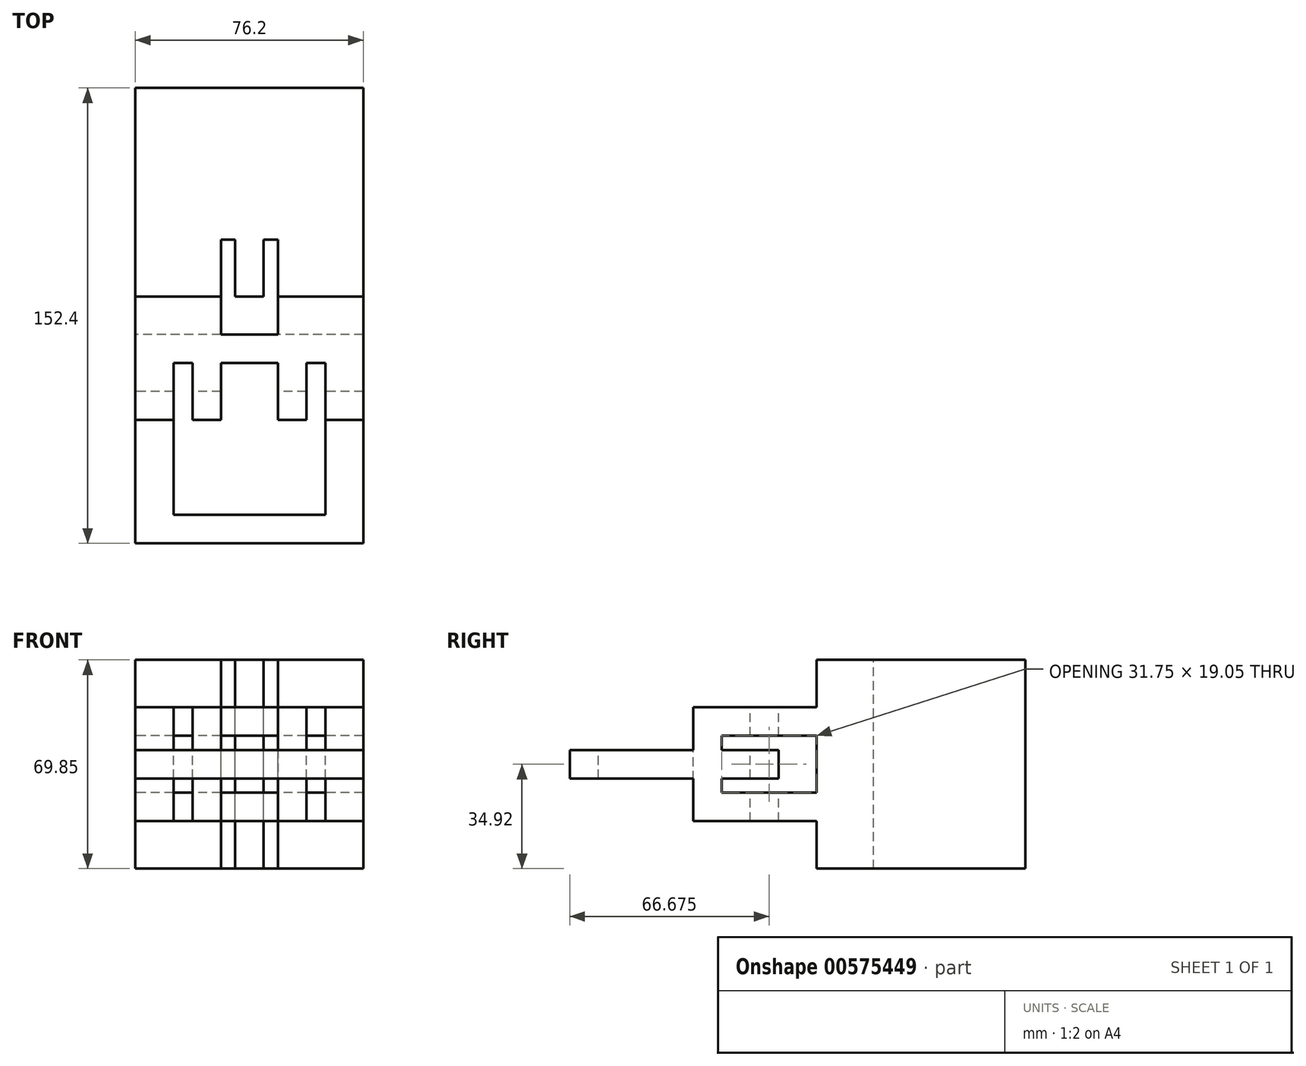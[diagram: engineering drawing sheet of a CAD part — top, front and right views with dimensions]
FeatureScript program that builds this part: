
annotation { "Feature Type Name" : "Feature", "Feature Type Description" : "" }
export const myFeature = defineFeature(function(context is Context, id is Id, definition is map)
    precondition{}
    {
        {
            var Q0;
            Q0=qCreatedBy(makeId("Top.planeOp"),FACE);
            var sketch = newSketch(context, id + "F0", { "sketchPlane" : qUnion([Q0])});
            skLineSegment(sketch, "E0.bottom", {"start": v(-38.1, 76.2) * mm, "end": v(38.1, 76.2) * mm});
            skLineSegment(sketch, "E0.top", {"start": v(-38.1, -76.2) * mm, "end": v(38.1, -76.2) * mm});
            skLineSegment(sketch, "E0.left", {"start": v(-38.1, 76.2) * mm, "end": v(-38.1, -76.2) * mm});
            skLineSegment(sketch, "E0.right", {"start": v(38.1, 76.2) * mm, "end": v(38.1, -76.2) * mm});
            skLineSegment(sketch, "E1", {"start": v(-38.1, 76.2) * mm, "end": v(38.1, -76.2) * mm, "construction": true});
            skSolve(sketch);
        }
        {
            var Q0;
            Q0=makeQuery(id+"F0.imprint","IMPRINT",FACE,{"disambiguationData":[TD([[makeQuery(id+"F0.imprint","IMPRINT",EDGE,{"derivedFrom":sQuery(id+"F0.wireOp",EDGE,"E0.bottom")}),-1.0]])]});
            extrude(context, id + "F1", {"entities" : qUnion([Q0]), "endBound" : BoundingType.SYMMETRIC, "oppositeDirection" : true, "depth" : 76.2 * mm, "offsetDistance" : 25.4 * mm});
        }
        {
            var Q0;
            Q0=makeQuery(id+"F1.opExtrude","CAP_FACE",FACE,{"disambiguationData":[OSD([sQuery(id+"F0.wireOp",EDGE,"E0.bottom"),sQuery(id+"F0.wireOp",EDGE,"E0.top"),sQuery(id+"F0.wireOp",EDGE,"E0.left"),sQuery(id+"F0.wireOp",EDGE,"E0.right")])],"isStart":true});
            var sketch = newSketch(context, id + "F2", { "sketchPlane" : qUnion([Q0])});
            skLineSegment(sketch, "E2.bottom", {"start": v(-34.92, -6.35) * mm, "end": v(34.92, -6.35) * mm});
            skLineSegment(sketch, "E2.top", {"start": v(-34.93, -76.2) * mm, "end": v(34.93, -76.2) * mm});
            skLineSegment(sketch, "E2.left", {"start": v(-34.92, -6.35) * mm, "end": v(-34.93, -76.2) * mm});
            skLineSegment(sketch, "E2.right", {"start": v(34.93, -6.35) * mm, "end": v(34.92, -76.2) * mm});
            skLineSegment(sketch, "E3.bottom", {"start": v(-4.76, 76.2) * mm, "end": v(4.76, 76.2) * mm});
            skLineSegment(sketch, "E3.top", {"start": v(-4.76, 6.35) * mm, "end": v(4.76, 6.35) * mm});
            skLineSegment(sketch, "E3.left", {"start": v(-4.76, 76.2) * mm, "end": v(-4.76, 6.35) * mm});
            skLineSegment(sketch, "E3.right", {"start": v(4.76, 76.2) * mm, "end": v(4.76, 6.35) * mm});
            skLineSegment(sketch, "E4.bottom", {"start": v(-25.4, -15.88) * mm, "end": v(25.4, -15.88) * mm});
            skLineSegment(sketch, "E4.top", {"start": v(-25.4, -66.68) * mm, "end": v(25.4, -66.68) * mm});
            skLineSegment(sketch, "E4.left", {"start": v(-25.4, -15.88) * mm, "end": v(-25.4, -66.68) * mm});
            skLineSegment(sketch, "E4.right", {"start": v(25.4, -15.88) * mm, "end": v(25.4, -66.68) * mm});
            skLineSegment(sketch, "E5", {"start": v(-9.52, -34.93) * mm, "end": v(-9.52, 25.4) * mm});
            skLineSegment(sketch, "E6", {"start": v(-9.52, 25.4) * mm, "end": v(9.53, 25.4) * mm});
            skLineSegment(sketch, "E7", {"start": v(9.53, 25.4) * mm, "end": v(9.53, -34.93) * mm});
            skLineSegment(sketch, "E8", {"start": v(9.53, -34.93) * mm, "end": v(19.05, -34.93) * mm});
            skLineSegment(sketch, "E9", {"start": v(19.05, -34.93) * mm, "end": v(19.05, 34.92) * mm});
            skLineSegment(sketch, "E10", {"start": v(19.05, 34.92) * mm, "end": v(-19.05, 34.92) * mm});
            skLineSegment(sketch, "E11", {"start": v(-19.05, 34.92) * mm, "end": v(-19.05, -34.93) * mm});
            skLineSegment(sketch, "E12", {"start": v(-19.05, -34.93) * mm, "end": v(-9.52, -34.93) * mm});
            skSolve(sketch);
        }
        {
            var Q0;
            {var subQ1=sQuery(id+"F2.wireOp",EDGE,"E3.top");Q0=makeQuery(id+"F2.imprint","IMPRINT",FACE,{"disambiguationData":[TD([[makeQuery(id+"F2.imprint","IMPRINT",EDGE,{"derivedFrom":subQ1}),-1.0]])]});}
            extrude(context, id + "F3", {"entities" : qUnion([Q0]), "operationType" : NewBodyOperationType.REMOVE, "endBound" : BoundingType.THROUGH_ALL, "oppositeDirection" : true, "depth" : 25.4 * mm, "offsetDistance" : 25.4 * mm});
        }
        {
            var Q0;
            Q0=makeQuery(id+"F1.opExtrude","SWEPT_FACE",FACE,{"disambiguationData":[OSD([sQuery(id+"F0.wireOp",EDGE,"E0.left")])]});
            var sketch = newSketch(context, id + "F4", { "sketchPlane" : qUnion([Q0])});
            skLineSegment(sketch, "E13.bottom", {"start": v(-6.35, 34.92) * mm, "end": v(-6.35, -34.92) * mm});
            skLineSegment(sketch, "E13.top", {"start": v(-76.2, 34.92) * mm, "end": v(-76.2, -34.93) * mm});
            skLineSegment(sketch, "E13.left", {"start": v(-6.35, 34.92) * mm, "end": v(-76.2, 34.92) * mm});
            skLineSegment(sketch, "E13.right", {"start": v(-6.35, -34.93) * mm, "end": v(-76.2, -34.93) * mm});
            skLineSegment(sketch, "E14.bottom", {"start": v(76.2, 4.76) * mm, "end": v(76.2, -4.76) * mm});
            skLineSegment(sketch, "E14.top", {"start": v(6.35, 4.76) * mm, "end": v(6.35, -4.76) * mm});
            skLineSegment(sketch, "E14.left", {"start": v(76.2, 4.76) * mm, "end": v(6.35, 4.76) * mm});
            skLineSegment(sketch, "E14.right", {"start": v(76.2, -4.76) * mm, "end": v(6.35, -4.76) * mm});
            skLineSegment(sketch, "E15.bottom", {"start": v(-15.87, 25.4) * mm, "end": v(-15.87, -25.4) * mm});
            skLineSegment(sketch, "E15.top", {"start": v(-66.67, 25.4) * mm, "end": v(-66.67, -25.4) * mm});
            skLineSegment(sketch, "E15.left", {"start": v(-15.87, 25.4) * mm, "end": v(-66.67, 25.4) * mm});
            skLineSegment(sketch, "E15.right", {"start": v(-15.87, -25.4) * mm, "end": v(-66.67, -25.4) * mm});
            skLineSegment(sketch, "E16", {"start": v(-34.92, 9.52) * mm, "end": v(25.4, 9.52) * mm});
            skLineSegment(sketch, "E17", {"start": v(25.4, 9.52) * mm, "end": v(25.4, -9.53) * mm});
            skLineSegment(sketch, "E18", {"start": v(25.4, -9.53) * mm, "end": v(-34.92, -9.53) * mm});
            skLineSegment(sketch, "E19", {"start": v(-34.92, -9.53) * mm, "end": v(-34.92, -19.05) * mm});
            skLineSegment(sketch, "E20", {"start": v(-34.92, -19.05) * mm, "end": v(34.93, -19.05) * mm});
            skLineSegment(sketch, "E21", {"start": v(34.93, -19.05) * mm, "end": v(34.93, 19.05) * mm});
            skLineSegment(sketch, "E22", {"start": v(34.93, 19.05) * mm, "end": v(-34.92, 19.05) * mm});
            skLineSegment(sketch, "E23", {"start": v(-34.92, 19.05) * mm, "end": v(-34.92, 9.52) * mm});
            skSolve(sketch);
        }
        {
            var Q0;
            {var subQ1=sQuery(id+"F4.wireOp",EDGE,"E14.top");Q0=makeQuery(id+"F4.imprint","IMPRINT",FACE,{"disambiguationData":[TD([[makeQuery(id+"F4.imprint","IMPRINT",EDGE,{"derivedFrom":subQ1}),-1.0]])]});}
            extrude(context, id + "F5", {"entities" : qUnion([Q0]), "operationType" : NewBodyOperationType.REMOVE, "endBound" : BoundingType.THROUGH_ALL, "oppositeDirection" : true, "depth" : 25.4 * mm, "offsetDistance" : 25.4 * mm});
        }
        {
            var Q0;
            Q0=makeQuery(id+"F2.imprint","IMPRINT",FACE,{"disambiguationData":[TD([[makeQuery(id+"F2.imprint","IMPRINT",EDGE,{"derivedFrom":sQuery(id+"F2.wireOp",EDGE,"E4.top")}),1.0]])]});
            var sketch = newSketch(context, id + "F6", { "sketchPlane" : qUnion([Q0])});
            skCircle(sketch, "E24", {"center": v(-22.62, -63.9) * mm, "radius": 2.78 * mm});
            skCircle(sketch, "E25", {"center": v(22.62, -63.9) * mm, "radius": 2.78 * mm});
            skCircle(sketch, "E26", {"center": v(22.62, -18.65) * mm, "radius": 2.78 * mm});
            skCircle(sketch, "E27", {"center": v(-22.62, -18.65) * mm, "radius": 2.78 * mm});
            skCircle(sketch, "E28", {"center": v(-6.75, -18.65) * mm, "radius": 2.78 * mm});
            skCircle(sketch, "E29", {"center": v(6.75, -18.65) * mm, "radius": 2.78 * mm});
            skCircle(sketch, "E30", {"center": v(-8.48, -37.5) * mm, "radius": 2.78 * mm});
            skCircle(sketch, "E31", {"center": v(8.22, -37.38) * mm, "radius": 2.78 * mm});
            skCircle(sketch, "E32", {"center": v(-19.14, -37.7) * mm, "radius": 2.78 * mm});
            skCircle(sketch, "E33", {"center": v(19.22, -37.7) * mm, "radius": 2.78 * mm});
            skSolve(sketch);
        }
        {
            var Q0;
            {var subQ0=sQuery(id+"F6.wireOp",EDGE,"E29");var subQ1=sQuery(id+"F2.wireOp",EDGE,"E4.bottom");var subQ4=makeQuery(id+"F6.imprint","INTERSECT",VERTEX,{"derivedFrom":[makeQuery(id+"F2.imprint","IMPRINT",EDGE,{"disambiguationData":[TD([[makeQuery(id+"F2.imprint","INTERSECT",VERTEX,{"derivedFrom":[subQ1,sQuery(id+"F2.wireOp",EDGE,"E5")]}),-1.0]])],"derivedFrom":subQ1}),subQ0]});Q0=makeQuery(id+"F6.imprint","IMPRINT",FACE,{"disambiguationData":[TD([[makeQuery(id+"F6.imprint","IMPRINT",EDGE,{"disambiguationData":[TD([[subQ4,1.0]])],"derivedFrom":subQ0}),1.0]])]});}
            var Q1;
            {var subQ0=sQuery(id+"F6.wireOp",EDGE,"E26");var subQ1=sQuery(id+"F2.wireOp",EDGE,"E4.right");var subQ4=makeQuery(id+"F6.imprint","INTERSECT",VERTEX,{"derivedFrom":[makeQuery(id+"F2.imprint","IMPRINT",EDGE,{"derivedFrom":subQ1}),subQ0]});Q1=makeQuery(id+"F6.imprint","IMPRINT",FACE,{"disambiguationData":[TD([[makeQuery(id+"F6.imprint","IMPRINT",EDGE,{"disambiguationData":[TD([[subQ4,-1.0]])],"derivedFrom":subQ0}),1.0]])]});}
            var Q2;
            Q2=makeQuery(id+"F6.imprint","IMPRINT",FACE,{"disambiguationData":[TD([[makeQuery(id+"F6.imprint","IMPRINT",EDGE,{"derivedFrom":sQuery(id+"F6.wireOp",EDGE,"E33")}),1.0]])]});
            var Q3;
            Q3=makeQuery(id+"F6.imprint","IMPRINT",FACE,{"disambiguationData":[TD([[makeQuery(id+"F6.imprint","IMPRINT",EDGE,{"derivedFrom":sQuery(id+"F6.wireOp",EDGE,"E31")}),1.0]])]});
            var Q4;
            Q4=makeQuery(id+"F6.imprint","IMPRINT",FACE,{"disambiguationData":[TD([[makeQuery(id+"F6.imprint","IMPRINT",EDGE,{"derivedFrom":sQuery(id+"F6.wireOp",EDGE,"E30")}),1.0]])]});
            var Q5;
            Q5=makeQuery(id+"F6.imprint","IMPRINT",FACE,{"disambiguationData":[TD([[makeQuery(id+"F6.imprint","IMPRINT",EDGE,{"derivedFrom":sQuery(id+"F6.wireOp",EDGE,"E32")}),1.0]])]});
            var Q6;
            {var subQ0=sQuery(id+"F6.wireOp",EDGE,"E28");var subQ1=sQuery(id+"F2.wireOp",EDGE,"E5");var subQ2=sQuery(id+"F2.wireOp",EDGE,"E4.bottom");var subQ3=makeQuery(id+"F2.imprint","INTERSECT",VERTEX,{"derivedFrom":[subQ2,subQ1]});var subQ4=makeQuery(id+"F6.imprint","INTERSECT",VERTEX,{"derivedFrom":[makeQuery(id+"F2.imprint","IMPRINT",EDGE,{"disambiguationData":[TD([[subQ3,-1.0]])],"derivedFrom":subQ2}),subQ0]});Q6=makeQuery(id+"F6.imprint","IMPRINT",FACE,{"disambiguationData":[TD([[makeQuery(id+"F6.imprint","IMPRINT",EDGE,{"disambiguationData":[TD([[subQ4,-1.0]])],"derivedFrom":subQ0}),1.0]])]});}
            var Q7;
            {var subQ0=sQuery(id+"F6.wireOp",EDGE,"E27");var subQ1=sQuery(id+"F2.wireOp",EDGE,"E4.left");var subQ4=makeQuery(id+"F6.imprint","INTERSECT",VERTEX,{"derivedFrom":[makeQuery(id+"F2.imprint","IMPRINT",EDGE,{"derivedFrom":subQ1}),subQ0]});Q7=makeQuery(id+"F6.imprint","IMPRINT",FACE,{"disambiguationData":[TD([[makeQuery(id+"F6.imprint","IMPRINT",EDGE,{"disambiguationData":[TD([[subQ4,1.0]])],"derivedFrom":subQ0}),1.0]])]});}
            var Q8;
            {var subQ0=sQuery(id+"F6.wireOp",EDGE,"E24");var subQ1=makeQuery(id+"F6.imprint","INTERSECT",VERTEX,{"derivedFrom":[makeQuery(id+"F2.imprint","IMPRINT",EDGE,{"derivedFrom":sQuery(id+"F2.wireOp",EDGE,"E4.top")}),subQ0]});Q8=makeQuery(id+"F6.imprint","IMPRINT",FACE,{"disambiguationData":[TD([[makeQuery(id+"F6.imprint","IMPRINT",EDGE,{"disambiguationData":[TD([[subQ1,1.0]])],"derivedFrom":subQ0}),1.0]])]});}
            var Q9;
            {var subQ0=sQuery(id+"F6.wireOp",EDGE,"E25");var subQ1=makeQuery(id+"F6.imprint","INTERSECT",VERTEX,{"derivedFrom":[makeQuery(id+"F2.imprint","IMPRINT",EDGE,{"derivedFrom":sQuery(id+"F2.wireOp",EDGE,"E4.top")}),subQ0]});Q9=makeQuery(id+"F6.imprint","IMPRINT",FACE,{"disambiguationData":[TD([[makeQuery(id+"F6.imprint","IMPRINT",EDGE,{"disambiguationData":[TD([[subQ1,1.0]])],"derivedFrom":subQ0}),1.0]])]});}
            extrude(context, id + "F7", {"entities" : qUnion([Q0, Q1, Q2, Q3, Q4, Q5, Q6, Q7, Q8, Q9]), "operationType" : NewBodyOperationType.REMOVE, "endBound" : BoundingType.THROUGH_ALL, "oppositeDirection" : true, "depth" : 25.4 * mm, "offsetDistance" : 25.4 * mm});
        }
        {
            var Q0;
            {var subQ5=sQuery(id+"F4.wireOp",EDGE,"E13.left");Q0=makeQuery(id+"F4.imprint","IMPRINT",FACE,{"disambiguationData":[TD([[makeQuery(id+"F4.imprint","IMPRINT",EDGE,{"derivedFrom":subQ5}),-1.0]])]});}
            var Q1;
            {var subQ8=sQuery(id+"F4.wireOp",EDGE,"E13.right");Q1=makeQuery(id+"F4.imprint","IMPRINT",FACE,{"disambiguationData":[TD([[makeQuery(id+"F4.imprint","IMPRINT",EDGE,{"derivedFrom":subQ8}),1.0]])]});}
            extrude(context, id + "F8", {"entities" : qUnion([Q0, Q1]), "operationType" : NewBodyOperationType.REMOVE, "endBound" : BoundingType.THROUGH_ALL, "oppositeDirection" : true, "depth" : 25.4 * mm, "offsetDistance" : 25.4 * mm});
        }
        {
            var Q0;
            Q0=makeQuery(id+"F2.imprint","IMPRINT",FACE,{"disambiguationData":[TD([[makeQuery(id+"F2.imprint","IMPRINT",EDGE,{"derivedFrom":sQuery(id+"F2.wireOp",EDGE,"E4.top")}),1.0]])]});
            extrude(context, id + "F9", {"entities" : qUnion([Q0]), "operationType" : NewBodyOperationType.REMOVE, "endBound" : BoundingType.THROUGH_ALL, "oppositeDirection" : true, "depth" : 25.4 * mm, "offsetDistance" : 25.4 * mm});
        }
    });
